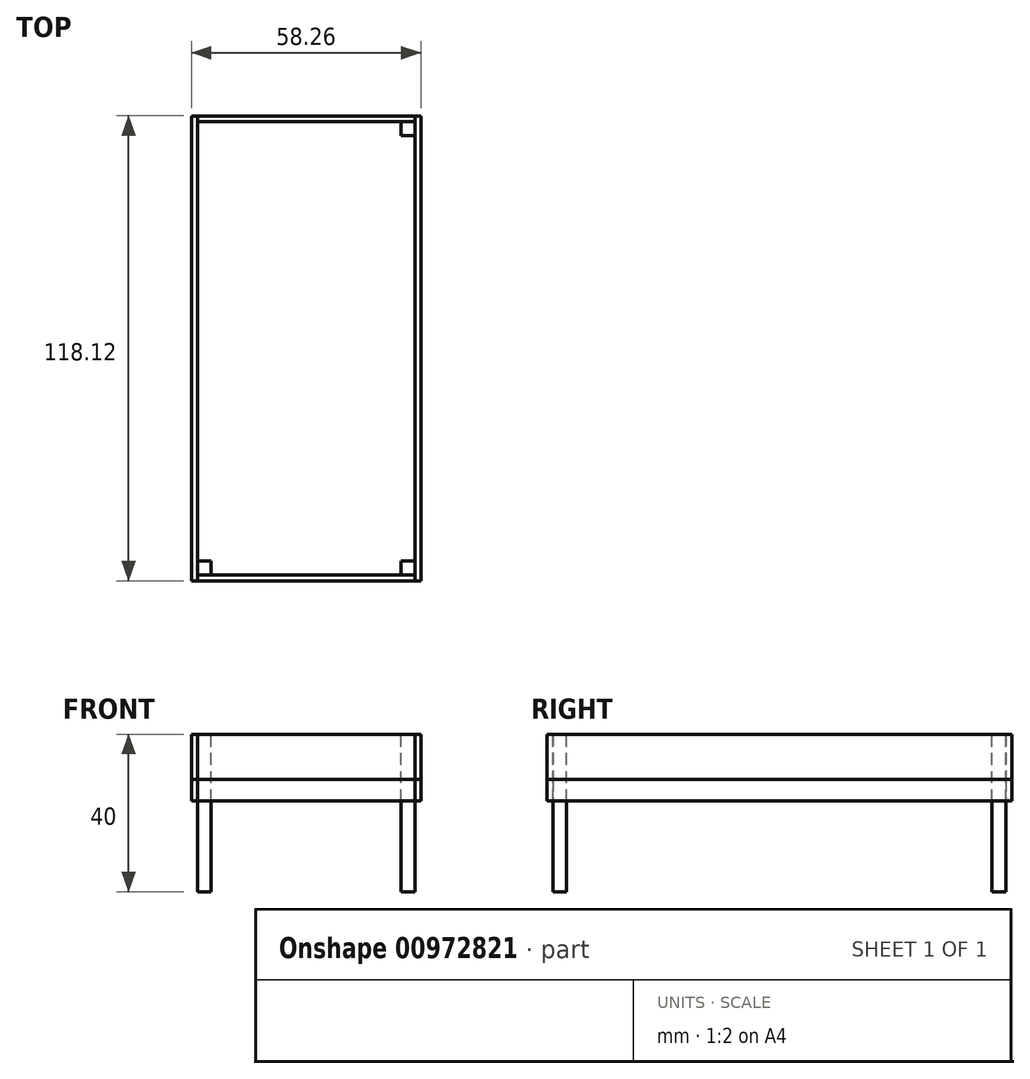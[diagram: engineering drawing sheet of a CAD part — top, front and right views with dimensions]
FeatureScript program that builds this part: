
annotation { "Feature Type Name" : "Feature", "Feature Type Description" : "" }
export const myFeature = defineFeature(function(context is Context, id is Id, definition is map)
    precondition{}
    {
        {
            var Q0;
            Q0=qCreatedBy(makeId("Top.planeOp"),FACE);
            var sketch = newSketch(context, id + "F0", { "sketchPlane" : qUnion([Q0])});
            skLineSegment(sketch, "E0.bottom", {"start": v(29.13, 59.06) * mm, "end": v(-29.13, 59.05) * mm});
            skLineSegment(sketch, "E0.top", {"start": v(29.13, -59.05) * mm, "end": v(-29.13, -59.06) * mm});
            skLineSegment(sketch, "E0.left", {"start": v(29.13, 59.06) * mm, "end": v(29.13, -59.05) * mm});
            skLineSegment(sketch, "E0.right", {"start": v(-29.13, 59.05) * mm, "end": v(-29.13, -59.06) * mm});
            skPoint(sketch, "E0.middle", {"position": v(0, 0) * mm});
            skSolve(sketch);
        }
        {
            var Q0;
            Q0=qCreatedBy(makeId("Front.planeOp"),FACE);
            var sketch = newSketch(context, id + "F1", { "sketchPlane" : qUnion([Q0])});
            skLineSegment(sketch, "E1.0", {"start": v(29.13, 0) * mm, "end": v(-29.13, 0) * mm});
            skLineSegment(sketch, "E2", {"start": v(-29.13, 0) * mm, "end": v(-29.13, -11.5) * mm});
            skLineSegment(sketch, "E3.MirrorCS", {"start": v(29.13, 0) * mm, "end": v(29.13, -11.5) * mm});
            skLineSegment(sketch, "E4", {"start": v(-29.13, -11.5) * mm, "end": v(29.13, -11.5) * mm});
            skLineSegment(sketch, "E5", {"start": v(0, 0) * mm, "end": v(0, -11.5) * mm, "construction": true});
            skLineSegment(sketch, "E6.0", {"start": v(-27.63, 0) * mm, "end": v(-27.63, -11.5) * mm});
            skLineSegment(sketch, "E7.0", {"start": v(27.63, 0) * mm, "end": v(27.63, -11.5) * mm});
            skLineSegment(sketch, "E8", {"start": v(0, 0) * mm, "end": v(0, -40) * mm, "construction": true});
            skLineSegment(sketch, "E9", {"start": v(-29.13, -11.5) * mm, "end": v(0, -40) * mm, "construction": true});
            skLineSegment(sketch, "E10", {"start": v(0, -40) * mm, "end": v(-29.13, -40) * mm, "construction": true});
            skLineSegment(sketch, "E11", {"start": v(-29.13, -40) * mm, "end": v(-29.13, -11.5) * mm, "construction": true});
            skLineSegment(sketch, "E12", {"start": v(-29.13, -11.5) * mm, "end": v(-29.13, -17) * mm});
            skLineSegment(sketch, "E13", {"start": v(-29.13, -17) * mm, "end": v(-27.63, -17) * mm});
            skLineSegment(sketch, "E14", {"start": v(-27.63, -17) * mm, "end": v(-27.63, -11.5) * mm});
            skLineSegment(sketch, "E15.MirrorCS", {"start": v(29.13, -17) * mm, "end": v(27.63, -17) * mm});
            skLineSegment(sketch, "E16.MirrorCS", {"start": v(27.63, -17) * mm, "end": v(27.63, -11.5) * mm});
            skLineSegment(sketch, "E17.MirrorCS", {"start": v(29.13, -11.5) * mm, "end": v(29.13, -17) * mm});
            skSolve(sketch);
        }
        {
            var Q0;
            {var subQ0=sQuery(id+"F1.wireOp",EDGE,"E2");Q0=makeQuery(id+"F1.imprint","IMPRINT",FACE,{"disambiguationData":[TD([[makeQuery(id+"F1.imprint","IMPRINT",EDGE,{"derivedFrom":subQ0}),1.0]])]});}
            var Q1;
            {var subQ0=sQuery(id+"F1.wireOp",EDGE,"E3.MirrorCS");Q1=makeQuery(id+"F1.imprint","IMPRINT",FACE,{"disambiguationData":[TD([[makeQuery(id+"F1.imprint","IMPRINT",EDGE,{"derivedFrom":subQ0}),-1.0]])]});}
            var Q2;
            Q2=sQuery(id+"F0.wireOp",VERTEX,"E0.top.end");
            var Q3;
            Q3=sQuery(id+"F0.wireOp",VERTEX,"E0.bottom.end");
            extrude(context, id + "F2", {"entities" : qUnion([Q0, Q1]), "endBound" : BoundingType.UP_TO_VERTEX, "depth" : 25 * mm, "endBoundEntityVertex" : qUnion([Q2]), "offsetDistance" : 25 * mm, "hasSecondDirection" : true, "secondDirectionBound" : SecondDirectionBoundingType.UP_TO_VERTEX, "secondDirectionOppositeDirection" : true, "secondDirectionDepth" : 25 * mm, "secondDirectionBoundEntityVertex" : qUnion([Q3])});
        }
        {
            var Q0;
            {var subQ0=sQuery(id+"F1.wireOp",EDGE,"E12");Q0=makeQuery(id+"F1.imprint","IMPRINT",FACE,{"disambiguationData":[TD([[makeQuery(id+"F1.imprint","IMPRINT",EDGE,{"derivedFrom":subQ0}),1.0]])]});}
            var Q1;
            Q1=makeQuery(id+"F1.imprint","IMPRINT",FACE,{"disambiguationData":[TD([[makeQuery(id+"F1.imprint","IMPRINT",EDGE,{"derivedFrom":sQuery(id+"F1.wireOp",EDGE,"E15.MirrorCS")}),-1.0]])]});
            var Q2;
            Q2=makeQuery(id+"F2.opExtrude","CAP_FACE",FACE,{"disambiguationData":[OSD([sQuery(id+"F1.wireOp",EDGE,"E1.0"),sQuery(id+"F1.wireOp",EDGE,"E2"),sQuery(id+"F1.wireOp",EDGE,"E4"),sQuery(id+"F1.wireOp",EDGE,"E6.0")])],"isStart":false});
            var Q3;
            Q3=makeQuery(id+"F2.opExtrude","CAP_FACE",FACE,{"disambiguationData":[OSD([sQuery(id+"F1.wireOp",EDGE,"E1.0"),sQuery(id+"F1.wireOp",EDGE,"E3.MirrorCS"),sQuery(id+"F1.wireOp",EDGE,"E4"),sQuery(id+"F1.wireOp",EDGE,"E7.0")])],"isStart":true});
            extrude(context, id + "F3", {"entities" : qUnion([Q0, Q1]), "endBound" : BoundingType.UP_TO_SURFACE, "depth" : 25 * mm, "endBoundEntityFace" : qUnion([Q2]), "offsetDistance" : 25 * mm, "hasSecondDirection" : true, "secondDirectionBound" : SecondDirectionBoundingType.UP_TO_SURFACE, "secondDirectionOppositeDirection" : true, "secondDirectionDepth" : 25 * mm, "secondDirectionBoundEntityFace" : qUnion([Q3])});
        }
        {
            var Q0;
            Q0=qCreatedBy(makeId("Right.planeOp"),FACE);
            var sketch = newSketch(context, id + "F4", { "sketchPlane" : qUnion([Q0])});
            skLineSegment(sketch, "E18", {"start": v(-59.05, 0) * mm, "end": v(-57.55, 0) * mm});
            skLineSegment(sketch, "E19", {"start": v(-57.55, 0) * mm, "end": v(-57.55, -11.5) * mm});
            skLineSegment(sketch, "E20", {"start": v(-59.05, 0) * mm, "end": v(-59.05, -11.5) * mm});
            skLineSegment(sketch, "E21", {"start": v(-59.05, -11.5) * mm, "end": v(-57.55, -11.5) * mm});
            skLineSegment(sketch, "E22.MirrorCS", {"start": v(59.05, 0) * mm, "end": v(57.55, 0) * mm});
            skLineSegment(sketch, "E23.MirrorCS", {"start": v(59.05, -11.5) * mm, "end": v(57.55, -11.5) * mm});
            skLineSegment(sketch, "E24.MirrorCS", {"start": v(59.05, 0) * mm, "end": v(59.05, -11.5) * mm});
            skLineSegment(sketch, "E25.MirrorCS", {"start": v(57.55, 0) * mm, "end": v(57.55, -11.5) * mm});
            skLineSegment(sketch, "E26", {"start": v(-59.05, -11.5) * mm, "end": v(-59.05, -17) * mm});
            skLineSegment(sketch, "E27", {"start": v(-59.05, -17) * mm, "end": v(-57.55, -17) * mm});
            skLineSegment(sketch, "E28", {"start": v(-57.55, -17) * mm, "end": v(-57.55, -11.5) * mm});
            skLineSegment(sketch, "E29.MirrorCS", {"start": v(59.05, -17) * mm, "end": v(57.55, -17) * mm});
            skLineSegment(sketch, "E30.MirrorCS", {"start": v(57.55, -17) * mm, "end": v(57.55, -11.5) * mm});
            skLineSegment(sketch, "E31.MirrorCS", {"start": v(59.05, -11.5) * mm, "end": v(59.05, -17) * mm});
            skSolve(sketch);
        }
        {
            var Q0;
            Q0=makeQuery(id+"F4.imprint","IMPRINT",FACE,{"disambiguationData":[TD([[makeQuery(id+"F4.imprint","IMPRINT",EDGE,{"derivedFrom":sQuery(id+"F4.wireOp",EDGE,"E22.MirrorCS")}),1.0]])]});
            var Q1;
            Q1=makeQuery(id+"F4.imprint","IMPRINT",FACE,{"disambiguationData":[TD([[makeQuery(id+"F4.imprint","IMPRINT",EDGE,{"derivedFrom":sQuery(id+"F4.wireOp",EDGE,"E18")}),-1.0]])]});
            var Q2;
            Q2=makeQuery(id+"F2.opExtrude","SWEPT_FACE",FACE,{"disambiguationData":[OSD([sQuery(id+"F1.wireOp",EDGE,"E7.0")])]});
            var Q3;
            Q3=makeQuery(id+"F2.opExtrude","SWEPT_FACE",FACE,{"disambiguationData":[OSD([sQuery(id+"F1.wireOp",EDGE,"E6.0")])]});
            extrude(context, id + "F5", {"entities" : qUnion([Q0, Q1]), "endBound" : BoundingType.UP_TO_SURFACE, "depth" : 25 * mm, "endBoundEntityFace" : qUnion([Q2]), "offsetDistance" : 25 * mm, "hasSecondDirection" : true, "secondDirectionBound" : SecondDirectionBoundingType.UP_TO_SURFACE, "secondDirectionOppositeDirection" : true, "secondDirectionDepth" : 25 * mm, "secondDirectionBoundEntityFace" : qUnion([Q3])});
        }
        {
            var Q0;
            Q0=makeQuery(id+"F4.imprint","IMPRINT",FACE,{"disambiguationData":[TD([[makeQuery(id+"F4.imprint","IMPRINT",EDGE,{"derivedFrom":sQuery(id+"F4.wireOp",EDGE,"E21")}),-1.0]])]});
            var Q1;
            Q1=makeQuery(id+"F4.imprint","IMPRINT",FACE,{"disambiguationData":[TD([[makeQuery(id+"F4.imprint","IMPRINT",EDGE,{"derivedFrom":sQuery(id+"F4.wireOp",EDGE,"E23.MirrorCS")}),1.0]])]});
            var Q2;
            Q2=makeQuery(id+"F3.opExtrude","SWEPT_FACE",FACE,{"disambiguationData":[OSD([sQuery(id+"F1.wireOp",EDGE,"E16.MirrorCS")])]});
            var Q3;
            Q3=makeQuery(id+"F3.opExtrude","SWEPT_FACE",FACE,{"disambiguationData":[OSD([sQuery(id+"F1.wireOp",EDGE,"E14")])]});
            extrude(context, id + "F6", {"entities" : qUnion([Q0, Q1]), "endBound" : BoundingType.UP_TO_SURFACE, "depth" : 25 * mm, "endBoundEntityFace" : qUnion([Q2]), "offsetDistance" : 25 * mm, "hasSecondDirection" : true, "secondDirectionBound" : SecondDirectionBoundingType.UP_TO_SURFACE, "secondDirectionOppositeDirection" : true, "secondDirectionDepth" : 25 * mm, "secondDirectionBoundEntityFace" : qUnion([Q3])});
        }
        {
            var Q0;
            Q0=qCreatedBy(makeId("Top.planeOp"),FACE);
            var sketch = newSketch(context, id + "F7", { "sketchPlane" : qUnion([Q0])});
            skLineSegment(sketch, "E32.0", {"start": v(-27.63, -59.06) * mm, "end": v(-27.63, 59.05) * mm});
            skLineSegment(sketch, "E33.0", {"start": v(27.63, 57.55) * mm, "end": v(-27.63, 57.55) * mm});
            skLineSegment(sketch, "E34.0", {"start": v(-29.13, 0) * mm, "end": v(29.13, 0) * mm});
            skLineSegment(sketch, "E35", {"start": v(0, 0) * mm, "end": v(0, 57.55) * mm, "construction": true});
            skLineSegment(sketch, "E36.bottom", {"start": v(-27.63, 57.55) * mm, "end": v(-24.13, 57.55) * mm});
            skLineSegment(sketch, "E36.top", {"start": v(-27.63, 54.05) * mm, "end": v(-24.13, 54.05) * mm});
            skLineSegment(sketch, "E36.left", {"start": v(-27.63, 57.55) * mm, "end": v(-27.63, 54.05) * mm});
            skLineSegment(sketch, "E36.right", {"start": v(-24.13, 57.55) * mm, "end": v(-24.13, 54.05) * mm});
            skLineSegment(sketch, "E37.MirrorCS", {"start": v(27.63, 54.05) * mm, "end": v(24.13, 54.05) * mm});
            skLineSegment(sketch, "E38.MirrorCS", {"start": v(27.63, 57.55) * mm, "end": v(24.13, 57.55) * mm});
            skLineSegment(sketch, "E39.MirrorCS", {"start": v(24.13, 57.55) * mm, "end": v(24.13, 54.05) * mm});
            skLineSegment(sketch, "E40.MirrorCS", {"start": v(27.63, 57.55) * mm, "end": v(27.63, 54.05) * mm});
            skLineSegment(sketch, "E41.MirrorCS", {"start": v(24.13, -57.55) * mm, "end": v(24.13, -54.05) * mm});
            skLineSegment(sketch, "E42.MirrorCS", {"start": v(27.63, -57.55) * mm, "end": v(27.63, -54.05) * mm});
            skLineSegment(sketch, "E43.MirrorCS", {"start": v(27.63, -57.55) * mm, "end": v(24.13, -57.55) * mm});
            skLineSegment(sketch, "E44.MirrorCS", {"start": v(27.63, -54.05) * mm, "end": v(24.13, -54.05) * mm});
            skLineSegment(sketch, "E45.MirrorCS", {"start": v(-24.13, -57.55) * mm, "end": v(-24.13, -54.05) * mm});
            skLineSegment(sketch, "E46.MirrorCS", {"start": v(-27.63, -57.55) * mm, "end": v(-27.63, -54.05) * mm});
            skLineSegment(sketch, "E47.MirrorCS", {"start": v(-27.63, -54.05) * mm, "end": v(-24.13, -54.05) * mm});
            skLineSegment(sketch, "E48.MirrorCS", {"start": v(-27.63, -57.55) * mm, "end": v(-24.13, -57.55) * mm});
            skSolve(sketch);
        }
        {
            var Q0;
            Q0=sQuery(id+"F1.wireOp",EDGE,"E10");
            cPlane(context, id + "F8", {"entities" : qUnion([Q0]), "cplaneType" : CPlaneType.LINE_ANGLE, "offset" : 25 * mm, "angle" : 90 * degree, "width" : 150 * mm, "height" : 150 * mm});
        }
        {
            var Q0;
            Q0=makeQuery(id+"F7.imprint","IMPRINT",FACE,{"disambiguationData":[TD([[makeQuery(id+"F7.imprint","IMPRINT",EDGE,{"derivedFrom":sQuery(id+"F7.wireOp",EDGE,"E36.bottom")}),-1.0]])]});
            var Q1;
            Q1=makeQuery(id+"F7.imprint","IMPRINT",FACE,{"disambiguationData":[TD([[makeQuery(id+"F7.imprint","IMPRINT",EDGE,{"derivedFrom":sQuery(id+"F7.wireOp",EDGE,"E37.MirrorCS")}),-1.0]])]});
            var Q2;
            Q2=makeQuery(id+"F7.imprint","IMPRINT",FACE,{"disambiguationData":[TD([[makeQuery(id+"F7.imprint","IMPRINT",EDGE,{"derivedFrom":sQuery(id+"F7.wireOp",EDGE,"E45.MirrorCS")}),1.0]])]});
            var Q3;
            Q3=makeQuery(id+"F7.imprint","IMPRINT",FACE,{"disambiguationData":[TD([[makeQuery(id+"F7.imprint","IMPRINT",EDGE,{"derivedFrom":sQuery(id+"F7.wireOp",EDGE,"E41.MirrorCS")}),-1.0]])]});
            var Q4;
            Q4=qCreatedBy(id+"F8.planeOp",FACE);
            extrude(context, id + "F9", {"entities" : qUnion([Q0, Q1, Q2, Q3]), "endBound" : BoundingType.UP_TO_SURFACE, "oppositeDirection" : true, "depth" : 40 * mm, "endBoundEntityFace" : qUnion([Q4]), "offsetDistance" : 25 * mm});
        }
    });
